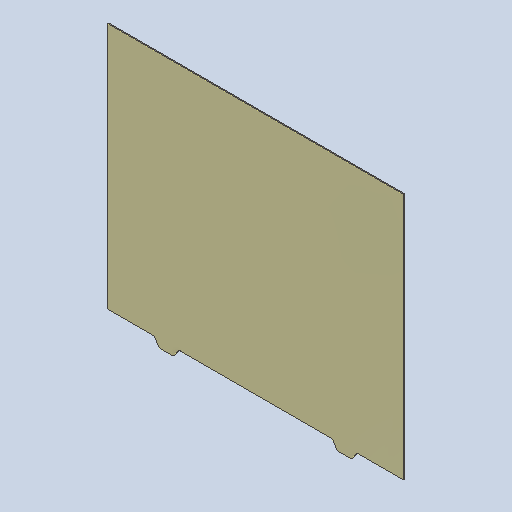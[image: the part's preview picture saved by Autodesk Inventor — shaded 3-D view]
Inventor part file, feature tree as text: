
AUTODESK INVENTOR PART (.ipt)
format: ipt  version: 2024 (Build 280153000, 153)  size: 287,744 bytes
history: native  units: mm
features: extrude x3, sketch x3, fillet x2, mirror x1, projected_geometry x1
ambient origin geometry x8: Origin, YZ Plane, XZ Plane, XY Plane, X Axis, Y Axis, Z Axis, Center Point
bodies: Solid1 (feature_tree), Solid2 (feature_tree)
feature tree (10):
  extrude  "Extrusion1"  Depth=250.0mm
  fillet  "Fillet1"  Radius=1.0mm
  extrude  "Extrusion3"  Depth=0.1mm TaperAngle=0.0deg
  mirror  "Mirror1"
  fillet  "Fillet2"  [1 undecoded]
  extrude  "Extrusion2"  Depth=8.0mm
  sketch  "Sketch1"  dims[d0=300.0mm d1=250.0mm d2=1.0mm d3=0.0mm]
  sketch  "Sketch2"  dims[d4=1.0mm d5=0.1mm d6=0.0mm d7=60.0deg]
  projected_geometry  "Projected Loop1"
  sketch  "Sketch3"  dims[d8=60.0deg d9=8.0mm d10=15.0mm d11=90.0mm d12=0.1mm d13=0.0mm d14=3.0mm]
note: 1 required parameter value undecoded (feature->parameter linkage not recoverable at this tier; creation-order binding heuristic only, values carry confidence <= 0.55)
